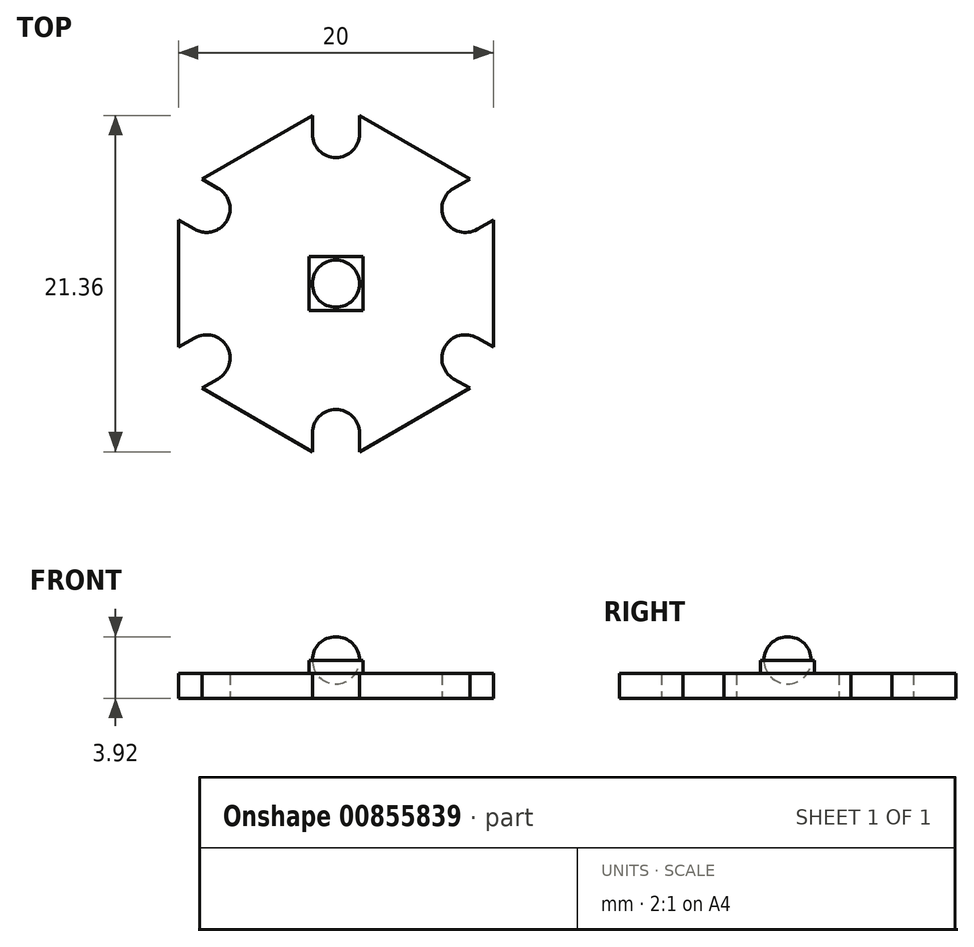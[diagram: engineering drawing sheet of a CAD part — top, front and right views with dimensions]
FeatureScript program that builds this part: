
annotation { "Feature Type Name" : "Feature", "Feature Type Description" : "" }
export const myFeature = defineFeature(function(context is Context, id is Id, definition is map)
    precondition{}
    {
        {
            var Q0;
            Q0=qCreatedBy(makeId("Top.planeOp"),FACE);
            var sketch = newSketch(context, id + "F0", { "sketchPlane" : qUnion([Q0])});
            skCircle(sketch, "E0.cCircle", {"center": v(0, 0) * mm, "radius": 10 * mm, "construction": true});
            skLineSegment(sketch, "E0.0", {"start": v(10, 4.04) * mm, "end": v(10, -4.04) * mm});
            skLineSegment(sketch, "E0.1", {"start": v(8.5, -6.64) * mm, "end": v(1.5, -10.68) * mm});
            skLineSegment(sketch, "E0.2", {"start": v(-1.5, -10.68) * mm, "end": v(-8.5, -6.64) * mm});
            skLineSegment(sketch, "E0.3", {"start": v(-10, -4.04) * mm, "end": v(-10, 4.04) * mm});
            skLineSegment(sketch, "E0.4", {"start": v(-8.5, 6.64) * mm, "end": v(-1.5, 10.68) * mm});
            skLineSegment(sketch, "E0.5", {"start": v(1.5, 10.68) * mm, "end": v(8.5, 6.64) * mm});
            skPoint(sketch, "E0.0.midPoint", {"position": v(10, 0) * mm});
            skArc(sketch, "E1", {"start": v(-1.5, 9.5) * mm, "mid": v(0, 8) * mm, "end": v(1.5, 9.5) * mm});
            skLineSegment(sketch, "E2", {"start": v(-1.5, 9.5) * mm, "end": v(-1.5, 10.68) * mm});
            skLineSegment(sketch, "E3.MirrorCS", {"start": v(1.5, 9.5) * mm, "end": v(1.5, 10.68) * mm});
            skPoint(sketch, "E4.orphan", {"position": v(0, 11.55) * mm});
            skPoint(sketch, "E5.1.0", {"position": v(-10, 5.77) * mm});
            skLineSegment(sketch, "E5.1.1", {"start": v(-7.48, 6.05) * mm, "end": v(-8.5, 6.64) * mm});
            skArc(sketch, "E5.1.2", {"start": v(-8.98, 3.45) * mm, "mid": v(-6.93, 4) * mm, "end": v(-7.48, 6.05) * mm});
            skLineSegment(sketch, "E5.1.3", {"start": v(-8.98, 3.45) * mm, "end": v(-10, 4.04) * mm});
            skPoint(sketch, "E5.2.0", {"position": v(-10, -5.77) * mm});
            skLineSegment(sketch, "E5.2.1", {"start": v(-8.98, -3.45) * mm, "end": v(-10, -4.04) * mm});
            skArc(sketch, "E5.2.2", {"start": v(-7.48, -6.05) * mm, "mid": v(-6.93, -4) * mm, "end": v(-8.98, -3.45) * mm});
            skLineSegment(sketch, "E5.2.3", {"start": v(-7.48, -6.05) * mm, "end": v(-8.5, -6.64) * mm});
            skPoint(sketch, "E5.3.0", {"position": v(0, -11.55) * mm});
            skLineSegment(sketch, "E5.3.1", {"start": v(-1.5, -9.5) * mm, "end": v(-1.5, -10.68) * mm});
            skArc(sketch, "E5.3.2", {"start": v(1.5, -9.5) * mm, "mid": v(0, -8) * mm, "end": v(-1.5, -9.5) * mm});
            skLineSegment(sketch, "E5.3.3", {"start": v(1.5, -9.5) * mm, "end": v(1.5, -10.68) * mm});
            skPoint(sketch, "E5.4.0", {"position": v(10, -5.77) * mm});
            skLineSegment(sketch, "E5.4.1", {"start": v(7.48, -6.05) * mm, "end": v(8.5, -6.64) * mm});
            skArc(sketch, "E5.4.2", {"start": v(8.98, -3.45) * mm, "mid": v(6.93, -4) * mm, "end": v(7.48, -6.05) * mm});
            skLineSegment(sketch, "E5.4.3", {"start": v(8.98, -3.45) * mm, "end": v(10, -4.04) * mm});
            skPoint(sketch, "E5.5.0", {"position": v(10, 5.77) * mm});
            skLineSegment(sketch, "E5.5.1", {"start": v(8.98, 3.45) * mm, "end": v(10, 4.04) * mm});
            skArc(sketch, "E5.5.2", {"start": v(7.48, 6.05) * mm, "mid": v(6.93, 4) * mm, "end": v(8.98, 3.45) * mm});
            skLineSegment(sketch, "E5.5.3", {"start": v(7.48, 6.05) * mm, "end": v(8.5, 6.64) * mm});
            skLineSegment(sketch, "E6.bottom", {"start": v(-1.71, 1.72) * mm, "end": v(1.71, 1.72) * mm});
            skLineSegment(sketch, "E6.top", {"start": v(-1.71, -1.72) * mm, "end": v(1.71, -1.72) * mm});
            skLineSegment(sketch, "E6.left", {"start": v(-1.72, 1.72) * mm, "end": v(-1.71, -1.72) * mm});
            skLineSegment(sketch, "E6.right", {"start": v(1.71, 1.72) * mm, "end": v(1.72, -1.71) * mm});
            skLineSegment(sketch, "E7", {"start": v(0, 1.72) * mm, "end": v(0, -1.72) * mm, "construction": true});
            skLineSegment(sketch, "E8", {"start": v(1.72, 0) * mm, "end": v(-1.72, 0) * mm, "construction": true});
            skCircle(sketch, "E9", {"center": v(0, 0) * mm, "radius": 1.5 * mm});
            skSolve(sketch);
        }
        {
            var Q0;
            Q0=makeQuery(id+"F0.imprint","IMPRINT",FACE,{"disambiguationData":[TD([[makeQuery(id+"F0.imprint","IMPRINT",EDGE,{"derivedFrom":sQuery(id+"F0.wireOp",EDGE,"E0.0")}),-1.0]])]});
            extrude(context, id + "F1", {"entities" : qUnion([Q0]), "depth" : 1.6 * mm, "offsetDistance" : 25.4 * mm});
        }
        {
            var Q0;
            Q0=makeQuery(id+"F0.imprint","IMPRINT",FACE,{"disambiguationData":[TD([[makeQuery(id+"F0.imprint","IMPRINT",EDGE,{"derivedFrom":sQuery(id+"F0.wireOp",EDGE,"E6.bottom")}),-1.0]])]});
            var Q1;
            Q1=makeQuery(id+"F0.imprint","IMPRINT",FACE,{"disambiguationData":[TD([[makeQuery(id+"F0.imprint","IMPRINT",EDGE,{"derivedFrom":sQuery(id+"F0.wireOp",EDGE,"E9")}),1.0]])]});
            extrude(context, id + "F2", {"entities" : qUnion([Q0, Q1]), "operationType" : NewBodyOperationType.ADD, "depth" : 2.42 * mm, "offsetDistance" : 25.4 * mm});
        }
        {
            var Q0;
            Q0=makeQuery(id+"F2.opExtrude","CAP_FACE",FACE,{"disambiguationData":[OSD([sQuery(id+"F0.wireOp",EDGE,"E6.bottom"),sQuery(id+"F0.wireOp",EDGE,"E6.top"),sQuery(id+"F0.wireOp",EDGE,"E6.left"),sQuery(id+"F0.wireOp",EDGE,"E6.right")])],"isStart":false});
            var sketch = newSketch(context, id + "F3", { "sketchPlane" : qUnion([Q0])});
            skArc(sketch, "E10", {"start": v(-1.5, 0) * mm, "mid": v(0, -1.5) * mm, "end": v(1.5, 0) * mm});
            skPoint(sketch, "E11.startSnap0", {"position": v(-1.72, 0) * mm});
            skPoint(sketch, "E11.endSnap0", {"position": v(-1.72, 0) * mm});
            skLineSegment(sketch, "E12", {"start": v(-1.5, 0) * mm, "end": v(1.5, 0) * mm});
            skSolve(sketch);
        }
        {
            var Q0;
            Q0 = qSketchRegion(id + "F3", true);
            var Q1;
            Q1=sQuery(id+"F3.wireOp",EDGE,"E12");
            revolve(context, id + "F4", {"surfaceOperationType" : NewSurfaceOperationType.NEW, "entities" : qUnion([Q0]), "axis" : qUnion([Q1]), "revolveType" : RevolveType.FULL});
        }
    });
